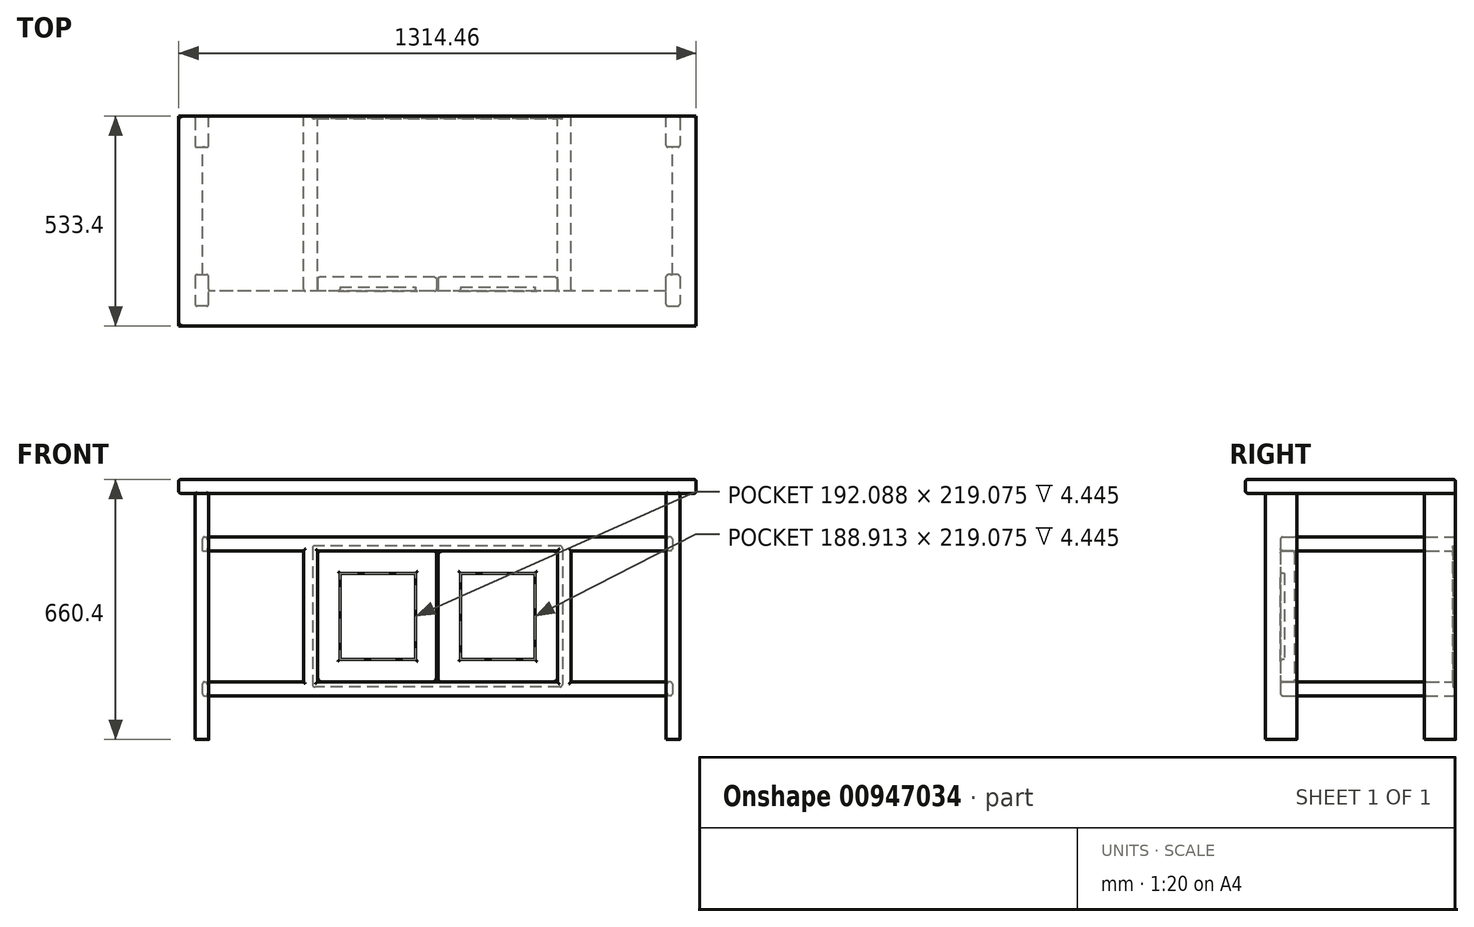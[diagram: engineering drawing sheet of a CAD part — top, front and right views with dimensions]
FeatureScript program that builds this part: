
annotation { "Feature Type Name" : "Feature", "Feature Type Description" : "" }
export const myFeature = defineFeature(function(context is Context, id is Id, definition is map)
    precondition{}
    {
        {
            var Q0;
            Q0=qCreatedBy(makeId("Front.planeOp"),FACE);
            var sketch = newSketch(context, id + "F0", { "sketchPlane" : qUnion([Q0])});
            skLineSegment(sketch, "E0.bottom", {"start": v(657.23, 660.4) * mm, "end": v(-657.23, 660.4) * mm});
            skLineSegment(sketch, "E0.top", {"start": v(657.22, 625.48) * mm, "end": v(-657.23, 625.48) * mm});
            skLineSegment(sketch, "E0.left", {"start": v(657.23, 660.4) * mm, "end": v(657.23, 625.48) * mm});
            skLineSegment(sketch, "E0.right", {"start": v(-657.23, 660.4) * mm, "end": v(-657.23, 625.48) * mm});
            skPoint(sketch, "E0.middle", {"position": v(0, 642.94) * mm});
            skLineSegment(sketch, "E1.bottom", {"start": v(596.9, 514.35) * mm, "end": v(-596.9, 514.35) * mm});
            skLineSegment(sketch, "E1.top", {"start": v(596.9, 479.43) * mm, "end": v(339.73, 479.43) * mm});
            skLineSegment(sketch, "E1.left", {"start": v(596.9, 514.35) * mm, "end": v(596.9, 479.43) * mm});
            skLineSegment(sketch, "E1.right", {"start": v(-596.9, 514.35) * mm, "end": v(-596.9, 479.43) * mm});
            skPoint(sketch, "E1.middle", {"position": v(0, 496.89) * mm});
            skLineSegment(sketch, "E2.bottom", {"start": v(596.9, 146.05) * mm, "end": v(339.73, 146.05) * mm});
            skLineSegment(sketch, "E2.top", {"start": v(596.9, 111.13) * mm, "end": v(-596.9, 111.13) * mm});
            skLineSegment(sketch, "E2.left", {"start": v(596.9, 146.05) * mm, "end": v(596.9, 111.13) * mm});
            skLineSegment(sketch, "E2.right", {"start": v(-596.9, 146.05) * mm, "end": v(-596.9, 111.13) * mm});
            skPoint(sketch, "E2.middle", {"position": v(0, 128.59) * mm});
            skLineSegment(sketch, "E3", {"start": v(304.8, 479.43) * mm, "end": v(304.8, 146.05) * mm});
            skLineSegment(sketch, "E4", {"start": v(339.73, 479.43) * mm, "end": v(339.73, 146.05) * mm});
            skLineSegment(sketch, "E5", {"start": v(0, 0) * mm, "end": v(0, -92.6) * mm, "construction": true});
            skLineSegment(sketch, "E6.MirrorCS", {"start": v(-304.8, 479.43) * mm, "end": v(-304.8, 146.05) * mm});
            skLineSegment(sketch, "E7.MirrorCS", {"start": v(-339.73, 479.43) * mm, "end": v(-339.73, 146.05) * mm});
            skLineSegment(sketch, "E8.trimOffspring", {"start": v(304.8, 479.43) * mm, "end": v(-304.8, 479.43) * mm});
            skLineSegment(sketch, "E9.trimOffspring", {"start": v(304.8, 146.05) * mm, "end": v(-304.8, 146.05) * mm});
            skLineSegment(sketch, "E10.trimOffspring", {"start": v(-339.73, 146.05) * mm, "end": v(-596.9, 146.05) * mm});
            skLineSegment(sketch, "E11.trimOffspring", {"start": v(-339.73, 479.43) * mm, "end": v(-596.9, 479.43) * mm});
            skLineSegment(sketch, "E12", {"start": v(304.8, 479.43) * mm, "end": v(339.73, 479.43) * mm, "construction": true});
            skSolve(sketch);
        }
        {
            var Q0;
            Q0=makeQuery(id+"F0.imprint","IMPRINT",FACE,{"disambiguationData":[TD([[makeQuery(id+"F0.imprint","IMPRINT",EDGE,{"derivedFrom":sQuery(id+"F0.wireOp",EDGE,"E1.bottom")}),1.0]])]});
            extrude(context, id + "F1", {"entities" : qUnion([Q0]), "depth" : 444.5 * mm, "offsetDistance" : 25.4 * mm});
        }
        {
            var Q0;
            Q0=makeQuery(id+"F0.imprint","IMPRINT",FACE,{"disambiguationData":[TD([[makeQuery(id+"F0.imprint","IMPRINT",EDGE,{"derivedFrom":sQuery(id+"F0.wireOp",EDGE,"E0.bottom")}),1.0]])]});
            extrude(context, id + "F2", {"entities" : qUnion([Q0]), "depth" : 533.4 * mm, "offsetDistance" : 25.4 * mm});
        }
        {
            var Q0;
            Q0=qCreatedBy(makeId("Top.planeOp"),FACE);
            var sketch = newSketch(context, id + "F3", { "sketchPlane" : qUnion([Q0])});
            skLineSegment(sketch, "E13.bottom", {"start": v(-615.95, -79.37) * mm, "end": v(-581.03, -79.37) * mm});
            skLineSegment(sketch, "E13.top", {"start": v(-615.95, 0) * mm, "end": v(-581.03, 0) * mm});
            skLineSegment(sketch, "E13.left", {"start": v(-615.95, -79.38) * mm, "end": v(-615.95, 0) * mm});
            skLineSegment(sketch, "E13.right", {"start": v(-581.03, -79.38) * mm, "end": v(-581.03, 0) * mm});
            skLineSegment(sketch, "E14.bottom", {"start": v(-615.95, -482.6) * mm, "end": v(-581.03, -482.6) * mm});
            skLineSegment(sketch, "E14.top", {"start": v(-615.95, -403.23) * mm, "end": v(-581.03, -403.23) * mm});
            skLineSegment(sketch, "E14.left", {"start": v(-615.95, -482.6) * mm, "end": v(-615.95, -403.23) * mm});
            skLineSegment(sketch, "E14.right", {"start": v(-581.03, -482.6) * mm, "end": v(-581.03, -403.23) * mm});
            skLineSegment(sketch, "E15", {"start": v(0, 0) * mm, "end": v(0, -190.92) * mm, "construction": true});
            skLineSegment(sketch, "E16.MirrorCS", {"start": v(615.95, -79.37) * mm, "end": v(581.03, -79.37) * mm});
            skLineSegment(sketch, "E17.MirrorCS", {"start": v(615.95, 0) * mm, "end": v(581.03, 0) * mm});
            skLineSegment(sketch, "E18.MirrorCS", {"start": v(615.95, -482.6) * mm, "end": v(581.03, -482.6) * mm});
            skLineSegment(sketch, "E19.MirrorCS", {"start": v(615.95, -403.23) * mm, "end": v(581.03, -403.23) * mm});
            skLineSegment(sketch, "E20.MirrorCS", {"start": v(581.03, -482.6) * mm, "end": v(581.03, -403.23) * mm});
            skLineSegment(sketch, "E21.MirrorCS", {"start": v(615.95, -79.38) * mm, "end": v(615.95, 0) * mm});
            skLineSegment(sketch, "E22.MirrorCS", {"start": v(615.95, -482.6) * mm, "end": v(615.95, -403.23) * mm});
            skLineSegment(sketch, "E23.MirrorCS", {"start": v(581.03, -79.38) * mm, "end": v(581.03, 0) * mm});
            skSolve(sketch);
        }
        {
            var Q0;
            Q0=qSketchRegion(id+"F3",true);
            var Q1;
            Q1=makeQuery(id+"F2.opExtrude","SWEPT_FACE",FACE,{"disambiguationData":[OSD([sQuery(id+"F0.wireOp",EDGE,"E0.top")])]});
            extrude(context, id + "F4", {"entities" : qUnion([Q0]), "operationType" : NewBodyOperationType.ADD, "endBound" : BoundingType.UP_TO_SURFACE, "depth" : 25.4 * mm, "endBoundEntityFace" : qUnion([Q1]), "offsetDistance" : 25.4 * mm});
        }
        {
            var Q0;
            Q0=makeQuery(id+"F4.boolean.opBoolean","MERGE",FACE,{"derivedFrom":[makeQuery(id+"F1.opExtrude","CAP_FACE",FACE,{"disambiguationData":[OSD([sQuery(id+"F0.wireOp",EDGE,"E1.bottom"),sQuery(id+"F0.wireOp",EDGE,"E1.top"),sQuery(id+"F0.wireOp",EDGE,"E1.left"),sQuery(id+"F0.wireOp",EDGE,"E1.right"),sQuery(id+"F0.wireOp",EDGE,"E2.bottom"),sQuery(id+"F0.wireOp",EDGE,"E2.top"),sQuery(id+"F0.wireOp",EDGE,"E2.left"),sQuery(id+"F0.wireOp",EDGE,"E2.right"),sQuery(id+"F0.wireOp",EDGE,"E3"),sQuery(id+"F0.wireOp",EDGE,"E4"),sQuery(id+"F0.wireOp",EDGE,"E6.MirrorCS"),sQuery(id+"F0.wireOp",EDGE,"E7.MirrorCS"),sQuery(id+"F0.wireOp",EDGE,"E8.trimOffspring"),sQuery(id+"F0.wireOp",EDGE,"E9.trimOffspring"),sQuery(id+"F0.wireOp",EDGE,"E10.trimOffspring"),sQuery(id+"F0.wireOp",EDGE,"E11.trimOffspring")])],"isStart":true}),makeQuery(id+"F2.opExtrude","CAP_FACE",FACE,{"disambiguationData":[OSD([sQuery(id+"F0.wireOp",EDGE,"E0.bottom"),sQuery(id+"F0.wireOp",EDGE,"E0.top"),sQuery(id+"F0.wireOp",EDGE,"E0.left"),sQuery(id+"F0.wireOp",EDGE,"E0.right")])],"isStart":true}),makeQuery(id+"F4.opExtrude","SWEPT_FACE",FACE,{"disambiguationData":[OSD([sQuery(id+"F3.wireOp",EDGE,"E13.top")])]}),makeQuery(id+"F4.opExtrude","SWEPT_FACE",FACE,{"disambiguationData":[OSD([sQuery(id+"F3.wireOp",EDGE,"E17.MirrorCS")])]})]});
            var sketch = newSketch(context, id + "F5", { "sketchPlane" : qUnion([Q0])});
            skLineSegment(sketch, "E24.0", {"start": v(-311.15, 492.13) * mm, "end": v(311.15, 492.13) * mm});
            skLineSegment(sketch, "E24.1", {"start": v(-317.5, 485.78) * mm, "end": v(-317.5, 139.7) * mm});
            skLineSegment(sketch, "E24.2", {"start": v(-311.15, 133.35) * mm, "end": v(311.15, 133.35) * mm});
            skLineSegment(sketch, "E24.3", {"start": v(317.5, 485.78) * mm, "end": v(317.5, 139.7) * mm});
            skPoint(sketch, "E25.visualSharp", {"position": v(-317.5, 492.13) * mm});
            skArc(sketch, "E25.filletArc", {"start": v(-311.15, 492.13) * mm, "mid": v(-315.64, 490.27) * mm, "end": v(-317.5, 485.78) * mm});
            skPoint(sketch, "E26.visualSharp", {"position": v(317.5, 492.13) * mm});
            skArc(sketch, "E26.filletArc", {"start": v(317.5, 485.78) * mm, "mid": v(315.64, 490.27) * mm, "end": v(311.15, 492.13) * mm});
            skPoint(sketch, "E27.visualSharp", {"position": v(317.5, 133.35) * mm});
            skArc(sketch, "E27.filletArc", {"start": v(311.15, 133.35) * mm, "mid": v(315.64, 135.2) * mm, "end": v(317.5, 139.7) * mm});
            skPoint(sketch, "E28.visualSharp", {"position": v(-317.5, 133.35) * mm});
            skArc(sketch, "E28.filletArc", {"start": v(-317.5, 139.7) * mm, "mid": v(-315.64, 135.2) * mm, "end": v(-311.15, 133.35) * mm});
            skSolve(sketch);
        }
        {
            var Q0;
            Q0=qSketchRegion(id+"F5",true);
            extrude(context, id + "F6", {"entities" : qUnion([Q0]), "oppositeDirection" : true, "depth" : 6.35 * mm, "offsetDistance" : 25.4 * mm});
        }
        {
            var Q0;
            Q0=makeQuery(id+"F6.opExtrude","SWEPT_BODY",BODY,{"disambiguationData":[OSD([sQuery(id+"F5.wireOp",EDGE,"E24.0"),sQuery(id+"F5.wireOp",EDGE,"E24.1"),sQuery(id+"F5.wireOp",EDGE,"E24.2"),sQuery(id+"F5.wireOp",EDGE,"E24.3"),sQuery(id+"F5.wireOp",EDGE,"E25.filletArc"),sQuery(id+"F5.wireOp",EDGE,"E26.filletArc"),sQuery(id+"F5.wireOp",EDGE,"E27.filletArc"),sQuery(id+"F5.wireOp",EDGE,"E28.filletArc")])]});
            var Q1;
            Q1=makeQuery(id+"F1.opExtrude","SWEPT_BODY",BODY,{"disambiguationData":[OSD([sQuery(id+"F0.wireOp",EDGE,"E1.bottom"),sQuery(id+"F0.wireOp",EDGE,"E1.top"),sQuery(id+"F0.wireOp",EDGE,"E1.left"),sQuery(id+"F0.wireOp",EDGE,"E1.right"),sQuery(id+"F0.wireOp",EDGE,"E2.bottom"),sQuery(id+"F0.wireOp",EDGE,"E2.top"),sQuery(id+"F0.wireOp",EDGE,"E2.left"),sQuery(id+"F0.wireOp",EDGE,"E2.right"),sQuery(id+"F0.wireOp",EDGE,"E3"),sQuery(id+"F0.wireOp",EDGE,"E4"),sQuery(id+"F0.wireOp",EDGE,"E6.MirrorCS"),sQuery(id+"F0.wireOp",EDGE,"E7.MirrorCS"),sQuery(id+"F0.wireOp",EDGE,"E8.trimOffspring"),sQuery(id+"F0.wireOp",EDGE,"E9.trimOffspring"),sQuery(id+"F0.wireOp",EDGE,"E10.trimOffspring"),sQuery(id+"F0.wireOp",EDGE,"E11.trimOffspring")])]});
            booleanBodies(context, id + "F7", {"operationType" : BooleanOperationType.SUBTRACTION, "tools" : qUnion([Q0]), "targets" : qUnion([Q1]), "keepTools" : true});
        }
        {
            var Q0;
            Q0=makeQuery(id+"F1.opExtrude","CAP_FACE",FACE,{"disambiguationData":[OSD([sQuery(id+"F0.wireOp",EDGE,"E1.bottom"),sQuery(id+"F0.wireOp",EDGE,"E1.top"),sQuery(id+"F0.wireOp",EDGE,"E1.left"),sQuery(id+"F0.wireOp",EDGE,"E1.right"),sQuery(id+"F0.wireOp",EDGE,"E2.bottom"),sQuery(id+"F0.wireOp",EDGE,"E2.top"),sQuery(id+"F0.wireOp",EDGE,"E2.left"),sQuery(id+"F0.wireOp",EDGE,"E2.right"),sQuery(id+"F0.wireOp",EDGE,"E3"),sQuery(id+"F0.wireOp",EDGE,"E4"),sQuery(id+"F0.wireOp",EDGE,"E6.MirrorCS"),sQuery(id+"F0.wireOp",EDGE,"E7.MirrorCS"),sQuery(id+"F0.wireOp",EDGE,"E8.trimOffspring"),sQuery(id+"F0.wireOp",EDGE,"E9.trimOffspring"),sQuery(id+"F0.wireOp",EDGE,"E10.trimOffspring"),sQuery(id+"F0.wireOp",EDGE,"E11.trimOffspring")])],"isStart":false});
            var sketch = newSketch(context, id + "F8", { "sketchPlane" : qUnion([Q0])});
            skLineSegment(sketch, "E29.bottom", {"start": v(-304.8, 479.43) * mm, "end": v(-1.59, 479.43) * mm});
            skLineSegment(sketch, "E29.top", {"start": v(-304.8, 146.05) * mm, "end": v(-1.59, 146.05) * mm});
            skLineSegment(sketch, "E29.left", {"start": v(-304.8, 479.43) * mm, "end": v(-304.8, 146.05) * mm});
            skLineSegment(sketch, "E29.right", {"start": v(-1.59, 479.43) * mm, "end": v(-1.59, 146.05) * mm});
            skLineSegment(sketch, "E30.bottom", {"start": v(1.59, 146.05) * mm, "end": v(304.8, 146.05) * mm});
            skLineSegment(sketch, "E30.top", {"start": v(1.59, 479.43) * mm, "end": v(304.8, 479.43) * mm});
            skLineSegment(sketch, "E30.left", {"start": v(1.59, 146.05) * mm, "end": v(1.59, 479.43) * mm});
            skLineSegment(sketch, "E30.right", {"start": v(304.8, 146.05) * mm, "end": v(304.8, 479.43) * mm});
            skLineSegment(sketch, "E31.0", {"start": v(-247.65, 422.28) * mm, "end": v(-55.56, 422.28) * mm});
            skLineSegment(sketch, "E31.1", {"start": v(-247.65, 422.28) * mm, "end": v(-247.65, 203.2) * mm});
            skLineSegment(sketch, "E31.2", {"start": v(-247.65, 203.2) * mm, "end": v(-55.56, 203.2) * mm});
            skLineSegment(sketch, "E31.3", {"start": v(-55.56, 203.2) * mm, "end": v(-55.56, 422.28) * mm});
            skLineSegment(sketch, "E32.0", {"start": v(58.74, 422.28) * mm, "end": v(247.65, 422.28) * mm});
            skLineSegment(sketch, "E32.1", {"start": v(58.74, 203.2) * mm, "end": v(58.74, 422.28) * mm});
            skLineSegment(sketch, "E32.2", {"start": v(58.74, 203.2) * mm, "end": v(247.65, 203.2) * mm});
            skLineSegment(sketch, "E32.3", {"start": v(247.65, 203.2) * mm, "end": v(247.65, 422.28) * mm});
            skPoint(sketch, "E33", {"position": v(0, 111.13) * mm});
            skSolve(sketch);
        }
        {
            var Q0;
            Q0=qSketchRegion(id+"F8",true);
            var Q1;
            Q1=makeQuery(id+"F8.imprint","IMPRINT",FACE,{"disambiguationData":[TD([[makeQuery(id+"F8.imprint","IMPRINT",EDGE,{"derivedFrom":sQuery(id+"F8.wireOp",EDGE,"E31.0")}),-1.0]])]});
            var Q2;
            Q2=makeQuery(id+"F8.imprint","IMPRINT",FACE,{"disambiguationData":[TD([[makeQuery(id+"F8.imprint","IMPRINT",EDGE,{"derivedFrom":sQuery(id+"F8.wireOp",EDGE,"E32.0")}),-1.0]])]});
            extrude(context, id + "F9", {"entities" : qUnion([Q0, Q1, Q2]), "oppositeDirection" : true, "depth" : 34.92 * mm, "offsetDistance" : 25.4 * mm});
        }
        {
            var Q0;
            Q0=makeQuery(id+"F8.imprint","IMPRINT",FACE,{"disambiguationData":[TD([[makeQuery(id+"F8.imprint","IMPRINT",EDGE,{"derivedFrom":sQuery(id+"F8.wireOp",EDGE,"E31.0")}),-1.0]])]});
            var Q1;
            Q1=makeQuery(id+"F8.imprint","IMPRINT",FACE,{"disambiguationData":[TD([[makeQuery(id+"F8.imprint","IMPRINT",EDGE,{"derivedFrom":sQuery(id+"F8.wireOp",EDGE,"E32.0")}),-1.0]])]});
            extrude(context, id + "F10", {"entities" : qUnion([Q0, Q1]), "operationType" : NewBodyOperationType.REMOVE, "oppositeDirection" : true, "depth" : 9.52 * mm, "offsetDistance" : 25.4 * mm});
        }
        {
            var Q0;
            Q0=makeQuery(id+"F2.opExtrude","SWEPT_FACE",FACE,{"disambiguationData":[OSD([sQuery(id+"F0.wireOp",EDGE,"E0.bottom")])]});
            var Q1;
            Q1=makeQuery(id+"F2.opExtrude","CAP_EDGE",EDGE,{"disambiguationData":[OSD([sQuery(id+"F0.wireOp",EDGE,"E0.top")])],"isStart":false});
            var Q2;
            Q2=makeQuery(id+"F2.opExtrude","SWEPT_EDGE",EDGE,{"disambiguationData":[OSD([sQuery(id+"F0.wireOp",EDGE,"E0.top"),sQuery(id+"F0.wireOp",EDGE,"E0.right")])]});
            var Q3;
            Q3=makeQuery(id+"F2.opExtrude","SWEPT_EDGE",EDGE,{"disambiguationData":[OSD([sQuery(id+"F0.wireOp",EDGE,"E0.top"),sQuery(id+"F0.wireOp",EDGE,"E0.left")])]});
            var Q4;
            Q4=makeQuery(id+"F1.opExtrude","CAP_EDGE",EDGE,{"disambiguationData":[OSD([sQuery(id+"F0.wireOp",EDGE,"E1.bottom")])],"isStart":false});
            var Q5;
            Q5=makeQuery(id+"F1.opExtrude","CAP_EDGE",EDGE,{"disambiguationData":[OSD([sQuery(id+"F0.wireOp",EDGE,"E1.top")])],"isStart":false});
            var Q6;
            Q6=makeQuery(id+"F1.opExtrude","SWEPT_EDGE",EDGE,{"disambiguationData":[OSD([sQuery(id+"F0.wireOp",EDGE,"E1.bottom"),sQuery(id+"F0.wireOp",EDGE,"E1.left")])]});
            var Q7;
            Q7=makeQuery(id+"F1.opExtrude","SWEPT_EDGE",EDGE,{"disambiguationData":[OSD([sQuery(id+"F0.wireOp",EDGE,"E1.top"),sQuery(id+"F0.wireOp",EDGE,"E1.left")])]});
            var Q8;
            Q8=makeQuery(id+"F1.opExtrude","CAP_EDGE",EDGE,{"disambiguationData":[OSD([sQuery(id+"F0.wireOp",EDGE,"E1.bottom")])],"isStart":true});
            var Q9;
            Q9=makeQuery(id+"F1.opExtrude","CAP_EDGE",EDGE,{"disambiguationData":[OSD([sQuery(id+"F0.wireOp",EDGE,"E1.top")])],"isStart":true});
            var Q10;
            Q10=makeQuery(id+"F1.opExtrude","CAP_EDGE",EDGE,{"disambiguationData":[OSD([sQuery(id+"F0.wireOp",EDGE,"E11.trimOffspring")])],"isStart":true});
            var Q11;
            Q11=makeQuery(id+"F1.opExtrude","SWEPT_EDGE",EDGE,{"disambiguationData":[OSD([sQuery(id+"F0.wireOp",EDGE,"E1.bottom"),sQuery(id+"F0.wireOp",EDGE,"E1.right")])]});
            var Q12;
            Q12=makeQuery(id+"F4.opExtrude","SWEPT_EDGE",EDGE,{"disambiguationData":[OSD([sQuery(id+"F3.wireOp",EDGE,"E13.bottom"),sQuery(id+"F3.wireOp",EDGE,"E13.left")])]});
            var Q13;
            Q13=makeQuery(id+"F4.opExtrude","SWEPT_EDGE",EDGE,{"disambiguationData":[OSD([sQuery(id+"F3.wireOp",EDGE,"E13.top"),sQuery(id+"F3.wireOp",EDGE,"E13.left")])]});
            var Q14;
            Q14=makeQuery(id+"F4.opExtrude","SWEPT_EDGE",EDGE,{"disambiguationData":[OSD([sQuery(id+"F3.wireOp",EDGE,"E14.top"),sQuery(id+"F3.wireOp",EDGE,"E14.left")])]});
            var Q15;
            Q15=makeQuery(id+"F4.opExtrude","SWEPT_EDGE",EDGE,{"disambiguationData":[OSD([sQuery(id+"F3.wireOp",EDGE,"E14.bottom"),sQuery(id+"F3.wireOp",EDGE,"E14.right")])]});
            var Q16;
            Q16=makeQuery(id+"F4.opExtrude","SWEPT_EDGE",EDGE,{"disambiguationData":[OSD([sQuery(id+"F3.wireOp",EDGE,"E14.bottom"),sQuery(id+"F3.wireOp",EDGE,"E14.left")])]});
            var Q17;
            Q17=makeQuery(id+"F4.opExtrude","SWEPT_EDGE",EDGE,{"disambiguationData":[OSD([sQuery(id+"F3.wireOp",EDGE,"E18.MirrorCS"),sQuery(id+"F3.wireOp",EDGE,"E20.MirrorCS")])]});
            var Q18;
            Q18=makeQuery(id+"F4.opExtrude","SWEPT_EDGE",EDGE,{"disambiguationData":[OSD([sQuery(id+"F3.wireOp",EDGE,"E18.MirrorCS"),sQuery(id+"F3.wireOp",EDGE,"E22.MirrorCS")])]});
            var Q19;
            Q19=makeQuery(id+"F4.opExtrude","SWEPT_EDGE",EDGE,{"disambiguationData":[OSD([sQuery(id+"F3.wireOp",EDGE,"E19.MirrorCS"),sQuery(id+"F3.wireOp",EDGE,"E22.MirrorCS")])]});
            var Q20;
            Q20=makeQuery(id+"F4.opExtrude","SWEPT_EDGE",EDGE,{"disambiguationData":[OSD([sQuery(id+"F3.wireOp",EDGE,"E16.MirrorCS"),sQuery(id+"F3.wireOp",EDGE,"E21.MirrorCS")])]});
            var Q21;
            Q21=makeQuery(id+"F4.opExtrude","SWEPT_EDGE",EDGE,{"disambiguationData":[OSD([sQuery(id+"F3.wireOp",EDGE,"E17.MirrorCS"),sQuery(id+"F3.wireOp",EDGE,"E21.MirrorCS")])]});
            var Q22;
            {var subQ0=sQuery(id+"F0.wireOp",EDGE,"E1.top");var subQ2=sQuery(id+"F3.wireOp",EDGE,"E17.MirrorCS");var subQ3=sQuery(id+"F3.wireOp",EDGE,"E23.MirrorCS");Q22=makeQuery(id+"F4.boolean.opBoolean","SPLIT",EDGE,{"disambiguationData":[TD([makeQuery(id+"F1.opExtrude","SWEPT_FACE",FACE,{"disambiguationData":[OSD([subQ0])]})])],"derivedFrom":makeQuery(id+"F4.opExtrude","SWEPT_EDGE",EDGE,{"disambiguationData":[OSD([subQ2,subQ3])]})});}
            var Q23;
            Q23=makeQuery(id+"F1.opExtrude","CAP_EDGE",EDGE,{"disambiguationData":[OSD([sQuery(id+"F0.wireOp",EDGE,"E2.bottom")])],"isStart":true});
            var Q24;
            Q24=makeQuery(id+"F1.opExtrude","CAP_EDGE",EDGE,{"disambiguationData":[OSD([sQuery(id+"F0.wireOp",EDGE,"E2.top")])],"isStart":true});
            var Q25;
            Q25=makeQuery(id+"F1.opExtrude","CAP_EDGE",EDGE,{"disambiguationData":[OSD([sQuery(id+"F0.wireOp",EDGE,"E4")])],"isStart":true});
            var Q26;
            {var subQ0=sQuery(id+"F3.wireOp",EDGE,"E16.MirrorCS");var subQ1=sQuery(id+"F3.wireOp",EDGE,"E23.MirrorCS");Q26=makeQuery(id+"F4.boolean.opBoolean","SPLIT",EDGE,{"disambiguationData":[TD([makeQuery(id+"F1.opExtrude","SWEPT_FACE",FACE,{"disambiguationData":[OSD([sQuery(id+"F0.wireOp",EDGE,"E1.bottom")])]})])],"derivedFrom":makeQuery(id+"F4.opExtrude","SWEPT_EDGE",EDGE,{"disambiguationData":[OSD([subQ0,subQ1])]})});}
            var Q27;
            {var subQ0=sQuery(id+"F3.wireOp",EDGE,"E23.MirrorCS");var subQ1=sQuery(id+"F3.wireOp",EDGE,"E16.MirrorCS");Q27=makeQuery(id+"F4.boolean.opBoolean","SPLIT",EDGE,{"disambiguationData":[TD([makeQuery(id+"F1.opExtrude","SWEPT_FACE",FACE,{"disambiguationData":[OSD([sQuery(id+"F0.wireOp",EDGE,"E1.top")])]})])],"derivedFrom":makeQuery(id+"F4.opExtrude","SWEPT_EDGE",EDGE,{"disambiguationData":[OSD([subQ1,subQ0])]})});}
            var Q28;
            {var subQ0=sQuery(id+"F3.wireOp",EDGE,"E16.MirrorCS");var subQ1=sQuery(id+"F3.wireOp",EDGE,"E23.MirrorCS");Q28=makeQuery(id+"F4.boolean.opBoolean","SPLIT",EDGE,{"disambiguationData":[TD([makeQuery(id+"F1.opExtrude","SWEPT_FACE",FACE,{"disambiguationData":[OSD([sQuery(id+"F0.wireOp",EDGE,"E2.top")])]})])],"derivedFrom":makeQuery(id+"F4.opExtrude","SWEPT_EDGE",EDGE,{"disambiguationData":[OSD([subQ0,subQ1])]})});}
            var Q29;
            {var subQ0=sQuery(id+"F3.wireOp",EDGE,"E23.MirrorCS");var subQ1=sQuery(id+"F3.wireOp",EDGE,"E17.MirrorCS");var subQ2=sQuery(id+"F0.wireOp",EDGE,"E2.top");Q29=makeQuery(id+"F4.boolean.opBoolean","SPLIT",EDGE,{"disambiguationData":[TD([makeQuery(id+"F1.opExtrude","SWEPT_FACE",FACE,{"disambiguationData":[OSD([subQ2])]})])],"derivedFrom":makeQuery(id+"F4.opExtrude","SWEPT_EDGE",EDGE,{"disambiguationData":[OSD([subQ1,subQ0])]})});}
            var Q30;
            {var subQ1=sQuery(id+"F0.wireOp",EDGE,"E1.bottom");var subQ2=sQuery(id+"F3.wireOp",EDGE,"E17.MirrorCS");var subQ3=sQuery(id+"F3.wireOp",EDGE,"E23.MirrorCS");Q30=makeQuery(id+"F4.boolean.opBoolean","SPLIT",EDGE,{"disambiguationData":[TD([makeQuery(id+"F1.opExtrude","SWEPT_FACE",FACE,{"disambiguationData":[OSD([subQ1])]})])],"derivedFrom":makeQuery(id+"F4.opExtrude","SWEPT_EDGE",EDGE,{"disambiguationData":[OSD([subQ2,subQ3])]})});}
            var Q31;
            Q31=makeQuery(id+"F1.opExtrude","CAP_EDGE",EDGE,{"disambiguationData":[OSD([sQuery(id+"F0.wireOp",EDGE,"E10.trimOffspring")])],"isStart":true});
            var Q32;
            Q32=makeQuery(id+"F1.opExtrude","CAP_EDGE",EDGE,{"disambiguationData":[OSD([sQuery(id+"F0.wireOp",EDGE,"E7.MirrorCS")])],"isStart":true});
            var Q33;
            {var subQ0=sQuery(id+"F0.wireOp",EDGE,"E0.top");Q33=makeQuery(id+"F4.boolean.opBoolean","SPLIT",EDGE,{"disambiguationData":[TD([makeQuery(id+"F4.opExtrude","SWEPT_FACE",FACE,{"disambiguationData":[OSD([sQuery(id+"F3.wireOp",EDGE,"E13.right")])]})])],"derivedFrom":makeQuery(id+"F2.opExtrude","CAP_EDGE",EDGE,{"disambiguationData":[OSD([subQ0])],"isStart":true})});}
            var Q34;
            {var subQ0=sQuery(id+"F0.wireOp",EDGE,"E0.top");var subQ1=sQuery(id+"F0.wireOp",EDGE,"E0.right");Q34=makeQuery(id+"F4.boolean.opBoolean","SPLIT",EDGE,{"disambiguationData":[TD([makeQuery(id+"F2.opExtrude","SWEPT_FACE",FACE,{"disambiguationData":[OSD([subQ1])]})])],"derivedFrom":makeQuery(id+"F2.opExtrude","CAP_EDGE",EDGE,{"disambiguationData":[OSD([subQ0])],"isStart":true})});}
            var Q35;
            {var subQ0=sQuery(id+"F0.wireOp",EDGE,"E0.left");var subQ1=sQuery(id+"F0.wireOp",EDGE,"E0.top");Q35=makeQuery(id+"F4.boolean.opBoolean","SPLIT",EDGE,{"disambiguationData":[TD([makeQuery(id+"F2.opExtrude","SWEPT_FACE",FACE,{"disambiguationData":[OSD([subQ0])]})])],"derivedFrom":makeQuery(id+"F2.opExtrude","CAP_EDGE",EDGE,{"disambiguationData":[OSD([subQ1])],"isStart":true})});}
            var Q36;
            {var subQ0=sQuery(id+"F0.wireOp",EDGE,"E10.trimOffspring");var subQ2=sQuery(id+"F3.wireOp",EDGE,"E13.top");var subQ3=sQuery(id+"F3.wireOp",EDGE,"E13.right");Q36=makeQuery(id+"F4.boolean.opBoolean","SPLIT",EDGE,{"disambiguationData":[TD([makeQuery(id+"F1.opExtrude","SWEPT_FACE",FACE,{"disambiguationData":[OSD([subQ0])]})])],"derivedFrom":makeQuery(id+"F4.opExtrude","SWEPT_EDGE",EDGE,{"disambiguationData":[OSD([subQ2,subQ3])]})});}
            var Q37;
            {var subQ0=sQuery(id+"F3.wireOp",EDGE,"E13.bottom");var subQ1=sQuery(id+"F3.wireOp",EDGE,"E13.right");Q37=makeQuery(id+"F4.boolean.opBoolean","SPLIT",EDGE,{"disambiguationData":[TD([makeQuery(id+"F1.opExtrude","SWEPT_FACE",FACE,{"disambiguationData":[OSD([sQuery(id+"F0.wireOp",EDGE,"E10.trimOffspring")])]})])],"derivedFrom":makeQuery(id+"F4.opExtrude","SWEPT_EDGE",EDGE,{"disambiguationData":[OSD([subQ0,subQ1])]})});}
            var Q38;
            {var subQ0=sQuery(id+"F3.wireOp",EDGE,"E13.bottom");var subQ1=sQuery(id+"F3.wireOp",EDGE,"E13.right");Q38=makeQuery(id+"F4.boolean.opBoolean","SPLIT",EDGE,{"disambiguationData":[TD([makeQuery(id+"F1.opExtrude","SWEPT_FACE",FACE,{"disambiguationData":[OSD([sQuery(id+"F0.wireOp",EDGE,"E1.bottom")])]})])],"derivedFrom":makeQuery(id+"F4.opExtrude","SWEPT_EDGE",EDGE,{"disambiguationData":[OSD([subQ0,subQ1])]})});}
            var Q39;
            {var subQ1=sQuery(id+"F3.wireOp",EDGE,"E13.top");var subQ2=sQuery(id+"F0.wireOp",EDGE,"E1.bottom");var subQ3=sQuery(id+"F3.wireOp",EDGE,"E13.right");Q39=makeQuery(id+"F4.boolean.opBoolean","SPLIT",EDGE,{"disambiguationData":[TD([makeQuery(id+"F1.opExtrude","SWEPT_FACE",FACE,{"disambiguationData":[OSD([subQ2])]})])],"derivedFrom":makeQuery(id+"F4.opExtrude","SWEPT_EDGE",EDGE,{"disambiguationData":[OSD([subQ1,subQ3])]})});}
            var Q40;
            {var subQ0=sQuery(id+"F3.wireOp",EDGE,"E14.top");var subQ1=sQuery(id+"F3.wireOp",EDGE,"E14.right");Q40=makeQuery(id+"F4.boolean.opBoolean","SPLIT",EDGE,{"disambiguationData":[TD([makeQuery(id+"F1.opExtrude","SWEPT_FACE",FACE,{"disambiguationData":[OSD([sQuery(id+"F0.wireOp",EDGE,"E10.trimOffspring")])]})])],"derivedFrom":makeQuery(id+"F4.opExtrude","SWEPT_EDGE",EDGE,{"disambiguationData":[OSD([subQ0,subQ1])]})});}
            var Q41;
            {var subQ0=sQuery(id+"F3.wireOp",EDGE,"E14.top");var subQ1=sQuery(id+"F3.wireOp",EDGE,"E14.right");Q41=makeQuery(id+"F4.boolean.opBoolean","SPLIT",EDGE,{"disambiguationData":[TD([makeQuery(id+"F1.opExtrude","SWEPT_FACE",FACE,{"disambiguationData":[OSD([sQuery(id+"F0.wireOp",EDGE,"E1.bottom")])]})])],"derivedFrom":makeQuery(id+"F4.opExtrude","SWEPT_EDGE",EDGE,{"disambiguationData":[OSD([subQ0,subQ1])]})});}
            var Q42;
            {var subQ0=sQuery(id+"F3.wireOp",EDGE,"E14.right");var subQ1=sQuery(id+"F3.wireOp",EDGE,"E14.top");Q42=makeQuery(id+"F4.boolean.opBoolean","SPLIT",EDGE,{"disambiguationData":[TD([makeQuery(id+"F1.opExtrude","SWEPT_FACE",FACE,{"disambiguationData":[OSD([sQuery(id+"F0.wireOp",EDGE,"E2.top")])]})])],"derivedFrom":makeQuery(id+"F4.opExtrude","SWEPT_EDGE",EDGE,{"disambiguationData":[OSD([subQ1,subQ0])]})});}
            var Q43;
            {var subQ0=sQuery(id+"F3.wireOp",EDGE,"E13.right");var subQ1=sQuery(id+"F3.wireOp",EDGE,"E13.top");var subQ2=sQuery(id+"F0.wireOp",EDGE,"E2.top");Q43=makeQuery(id+"F4.boolean.opBoolean","SPLIT",EDGE,{"disambiguationData":[TD([makeQuery(id+"F1.opExtrude","SWEPT_FACE",FACE,{"disambiguationData":[OSD([subQ2])]})])],"derivedFrom":makeQuery(id+"F4.opExtrude","SWEPT_EDGE",EDGE,{"disambiguationData":[OSD([subQ1,subQ0])]})});}
            var Q44;
            {var subQ0=sQuery(id+"F3.wireOp",EDGE,"E13.bottom");var subQ1=sQuery(id+"F3.wireOp",EDGE,"E13.right");Q44=makeQuery(id+"F4.boolean.opBoolean","SPLIT",EDGE,{"disambiguationData":[TD([makeQuery(id+"F1.opExtrude","SWEPT_FACE",FACE,{"disambiguationData":[OSD([sQuery(id+"F0.wireOp",EDGE,"E2.top")])]})])],"derivedFrom":makeQuery(id+"F4.opExtrude","SWEPT_EDGE",EDGE,{"disambiguationData":[OSD([subQ0,subQ1])]})});}
            var Q45;
            {var subQ0=sQuery(id+"F3.wireOp",EDGE,"E20.MirrorCS");var subQ1=sQuery(id+"F3.wireOp",EDGE,"E19.MirrorCS");Q45=makeQuery(id+"F4.boolean.opBoolean","SPLIT",EDGE,{"disambiguationData":[TD([makeQuery(id+"F1.opExtrude","SWEPT_FACE",FACE,{"disambiguationData":[OSD([sQuery(id+"F0.wireOp",EDGE,"E1.bottom")])]})])],"derivedFrom":makeQuery(id+"F4.opExtrude","SWEPT_EDGE",EDGE,{"disambiguationData":[OSD([subQ1,subQ0])]})});}
            var Q46;
            {var subQ0=sQuery(id+"F3.wireOp",EDGE,"E19.MirrorCS");var subQ1=sQuery(id+"F3.wireOp",EDGE,"E20.MirrorCS");Q46=makeQuery(id+"F4.boolean.opBoolean","SPLIT",EDGE,{"disambiguationData":[TD([makeQuery(id+"F1.opExtrude","SWEPT_FACE",FACE,{"disambiguationData":[OSD([sQuery(id+"F0.wireOp",EDGE,"E1.top")])]})])],"derivedFrom":makeQuery(id+"F4.opExtrude","SWEPT_EDGE",EDGE,{"disambiguationData":[OSD([subQ0,subQ1])]})});}
            var Q47;
            {var subQ0=sQuery(id+"F3.wireOp",EDGE,"E20.MirrorCS");var subQ1=sQuery(id+"F3.wireOp",EDGE,"E19.MirrorCS");Q47=makeQuery(id+"F4.boolean.opBoolean","SPLIT",EDGE,{"disambiguationData":[TD([makeQuery(id+"F1.opExtrude","SWEPT_FACE",FACE,{"disambiguationData":[OSD([sQuery(id+"F0.wireOp",EDGE,"E2.top")])]})])],"derivedFrom":makeQuery(id+"F4.opExtrude","SWEPT_EDGE",EDGE,{"disambiguationData":[OSD([subQ1,subQ0])]})});}
            var Q48;
            Q48=makeQuery(id+"F1.opExtrude","CAP_EDGE",EDGE,{"disambiguationData":[OSD([sQuery(id+"F0.wireOp",EDGE,"E2.top")])],"isStart":false});
            var Q49;
            Q49=makeQuery(id+"F1.opExtrude","CAP_EDGE",EDGE,{"disambiguationData":[OSD([sQuery(id+"F0.wireOp",EDGE,"E2.bottom")])],"isStart":false});
            var Q50;
            Q50=makeQuery(id+"F1.opExtrude","CAP_EDGE",EDGE,{"disambiguationData":[OSD([sQuery(id+"F0.wireOp",EDGE,"E4")])],"isStart":false});
            var Q51;
            Q51=makeQuery(id+"F1.opExtrude","CAP_EDGE",EDGE,{"disambiguationData":[OSD([sQuery(id+"F0.wireOp",EDGE,"E7.MirrorCS")])],"isStart":false});
            var Q52;
            Q52=makeQuery(id+"F1.opExtrude","CAP_EDGE",EDGE,{"disambiguationData":[OSD([sQuery(id+"F0.wireOp",EDGE,"E11.trimOffspring")])],"isStart":false});
            var Q53;
            Q53=makeQuery(id+"F1.opExtrude","CAP_EDGE",EDGE,{"disambiguationData":[OSD([sQuery(id+"F0.wireOp",EDGE,"E10.trimOffspring")])],"isStart":false});
            var Q54;
            Q54=makeQuery(id+"F1.opExtrude","SWEPT_EDGE",EDGE,{"disambiguationData":[OSD([sQuery(id+"F0.wireOp",EDGE,"E2.bottom"),sQuery(id+"F0.wireOp",EDGE,"E2.left")])]});
            var Q55;
            Q55=makeQuery(id+"F1.opExtrude","SWEPT_EDGE",EDGE,{"disambiguationData":[OSD([sQuery(id+"F0.wireOp",EDGE,"E2.top"),sQuery(id+"F0.wireOp",EDGE,"E2.left")])]});
            var Q56;
            Q56=makeQuery(id+"F1.opExtrude","SWEPT_EDGE",EDGE,{"disambiguationData":[OSD([sQuery(id+"F0.wireOp",EDGE,"E2.right"),sQuery(id+"F0.wireOp",EDGE,"E10.trimOffspring")])]});
            var Q57;
            Q57=makeQuery(id+"F1.opExtrude","SWEPT_EDGE",EDGE,{"disambiguationData":[OSD([sQuery(id+"F0.wireOp",EDGE,"E2.top"),sQuery(id+"F0.wireOp",EDGE,"E2.right")])]});
            var Q58;
            Q58=makeQuery(id+"F1.opExtrude","CAP_EDGE",EDGE,{"disambiguationData":[OSD([sQuery(id+"F0.wireOp",EDGE,"E6.MirrorCS")])],"isStart":false});
            var Q59;
            Q59=makeQuery(id+"F1.opExtrude","CAP_EDGE",EDGE,{"disambiguationData":[OSD([sQuery(id+"F0.wireOp",EDGE,"E8.trimOffspring")])],"isStart":false});
            var Q60;
            Q60=makeQuery(id+"F1.opExtrude","CAP_EDGE",EDGE,{"disambiguationData":[OSD([sQuery(id+"F0.wireOp",EDGE,"E3")])],"isStart":false});
            var Q61;
            Q61=makeQuery(id+"F1.opExtrude","CAP_EDGE",EDGE,{"disambiguationData":[OSD([sQuery(id+"F0.wireOp",EDGE,"E9.trimOffspring")])],"isStart":false});
            fillet(context, id + "F11", {"entities" : qUnion([Q0, Q1, Q2, Q3, Q4, Q5, Q6, Q7, Q8, Q9, Q10, Q11, Q12, Q13, Q14, Q15, Q16, Q17, Q18, Q19, Q20, Q21, Q22, Q23, Q24, Q25, Q26, Q27, Q28, Q29, Q30, Q31, Q32, Q33, Q34, Q35, Q36, Q37, Q38, Q39, Q40, Q41, Q42, Q43, Q44, Q45, Q46, Q47, Q48, Q49, Q50, Q51, Q52, Q53, Q54, Q55, Q56, Q57, Q58, Q59, Q60, Q61]), "radius" : 5.08 * mm, "tangentPropagation" : true, "allowEdgeOverflow" : false});
        }
        {
            var Q0;
            Q0=makeQuery(id+"F9.opExtrude","CAP_FACE",FACE,{"disambiguationData":[OSD([sQuery(id+"F8.wireOp",EDGE,"E29.bottom"),sQuery(id+"F8.wireOp",EDGE,"E29.top"),sQuery(id+"F8.wireOp",EDGE,"E29.left"),sQuery(id+"F8.wireOp",EDGE,"E29.right")])],"isStart":true});
            var Q1;
            Q1=makeQuery(id+"F9.opExtrude","CAP_FACE",FACE,{"disambiguationData":[OSD([sQuery(id+"F8.wireOp",EDGE,"E30.bottom"),sQuery(id+"F8.wireOp",EDGE,"E30.top"),sQuery(id+"F8.wireOp",EDGE,"E30.left"),sQuery(id+"F8.wireOp",EDGE,"E30.right")])],"isStart":true});
            var Q2;
            Q2=makeQuery(id+"F9.opExtrude","CAP_FACE",FACE,{"disambiguationData":[OSD([sQuery(id+"F8.wireOp",EDGE,"E30.bottom"),sQuery(id+"F8.wireOp",EDGE,"E30.top"),sQuery(id+"F8.wireOp",EDGE,"E30.left"),sQuery(id+"F8.wireOp",EDGE,"E30.right")])],"isStart":false});
            var Q3;
            Q3=makeQuery(id+"F9.opExtrude","CAP_FACE",FACE,{"disambiguationData":[OSD([sQuery(id+"F8.wireOp",EDGE,"E29.bottom"),sQuery(id+"F8.wireOp",EDGE,"E29.top"),sQuery(id+"F8.wireOp",EDGE,"E29.left"),sQuery(id+"F8.wireOp",EDGE,"E29.right")])],"isStart":false});
            fillet(context, id + "F12", {"entities" : qUnion([Q0, Q1, Q2, Q3]), "radius" : 5.08 * mm, "tangentPropagation" : true, "allowEdgeOverflow" : false});
        }
    });
